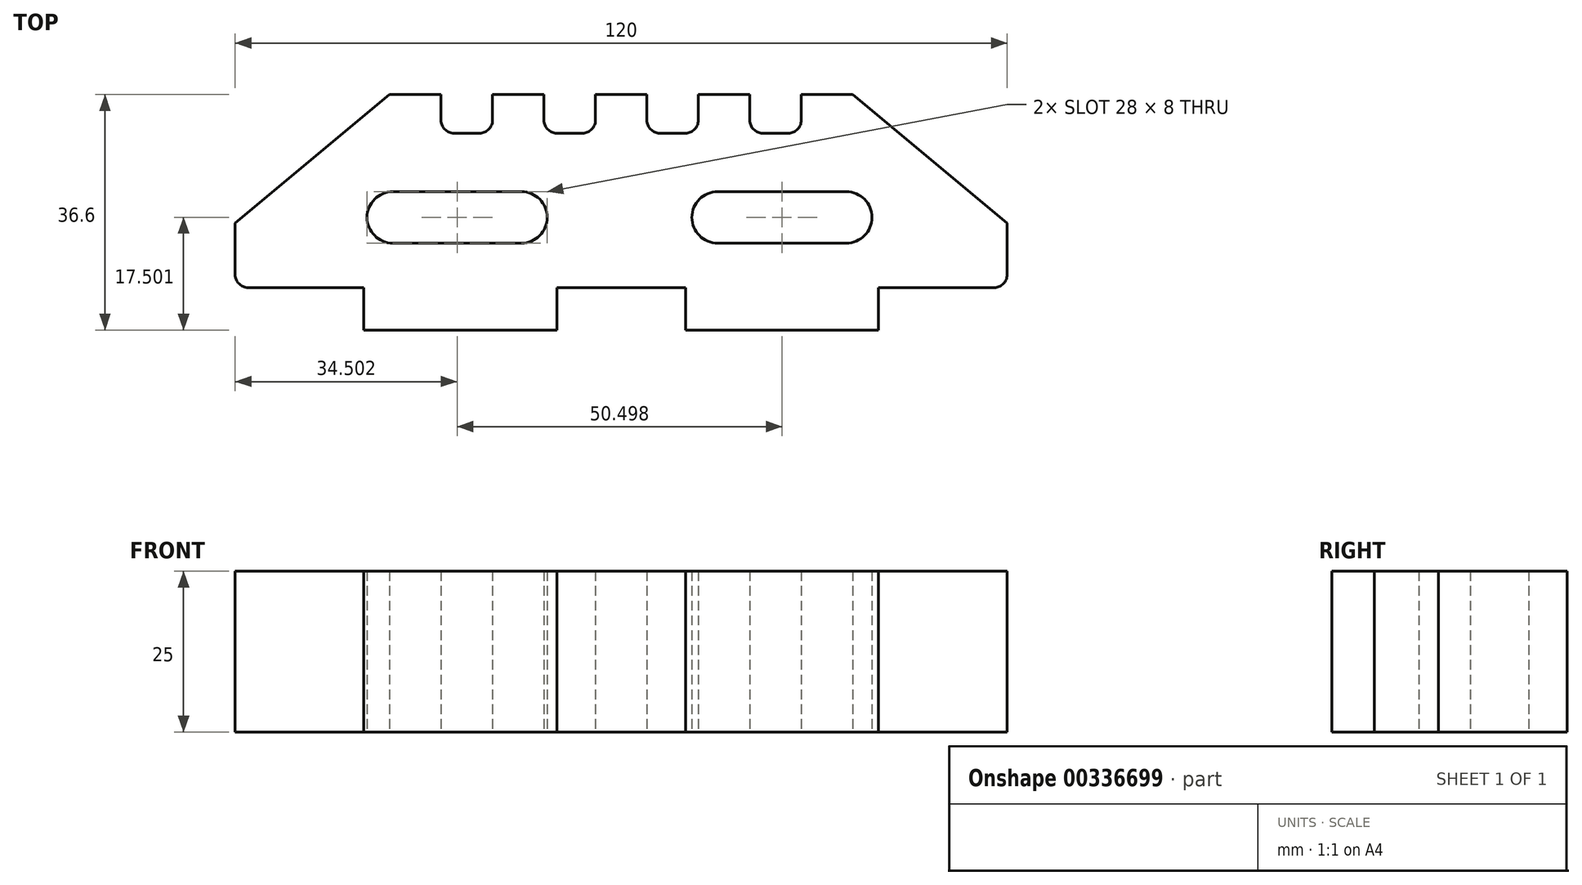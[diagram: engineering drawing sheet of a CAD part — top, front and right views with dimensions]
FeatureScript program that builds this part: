
annotation { "Feature Type Name" : "Feature", "Feature Type Description" : "" }
export const myFeature = defineFeature(function(context is Context, id is Id, definition is map)
    precondition{}
    {
        {
            var Q0;
            Q0=qCreatedBy(makeId("Top.planeOp"),FACE);
            var sketch = newSketch(context, id + "F0", { "sketchPlane" : qUnion([Q0])});
            skLineSegment(sketch, "E0", {"start": v(-86, -8.4) * mm, "end": v(-68, -8.4) * mm});
            skLineSegment(sketch, "E1", {"start": v(-68, -8.4) * mm, "end": v(-68, -15) * mm});
            skLineSegment(sketch, "E2", {"start": v(-68, -15) * mm, "end": v(-38, -15) * mm});
            skLineSegment(sketch, "E3", {"start": v(-38, -8.4) * mm, "end": v(-38, -15) * mm});
            skLineSegment(sketch, "E4", {"start": v(-38, -8.4) * mm, "end": v(-18, -8.4) * mm});
            skLineSegment(sketch, "E5", {"start": v(-18, -8.4) * mm, "end": v(-18, -15) * mm});
            skLineSegment(sketch, "E6", {"start": v(-18, -15) * mm, "end": v(12, -15) * mm});
            skLineSegment(sketch, "E7", {"start": v(12, -15) * mm, "end": v(12, -8.4) * mm});
            skLineSegment(sketch, "E8", {"start": v(12, -8.4) * mm, "end": v(30, -8.4) * mm});
            skLineSegment(sketch, "E9", {"start": v(-88, -6.4) * mm, "end": v(-88, 1.6) * mm});
            skLineSegment(sketch, "E10", {"start": v(-88, 1.6) * mm, "end": v(-64, 21.6) * mm});
            skLineSegment(sketch, "E11", {"start": v(-64, 21.6) * mm, "end": v(-56, 21.6) * mm});
            skLineSegment(sketch, "E12", {"start": v(-56, 21.6) * mm, "end": v(-56, 17.6) * mm});
            skLineSegment(sketch, "E13", {"start": v(-54, 15.6) * mm, "end": v(-50, 15.6) * mm});
            skLineSegment(sketch, "E14", {"start": v(-48, 17.6) * mm, "end": v(-48, 21.6) * mm});
            skLineSegment(sketch, "E15", {"start": v(-48, 21.6) * mm, "end": v(-40, 21.6) * mm});
            skLineSegment(sketch, "E16", {"start": v(-40, 21.6) * mm, "end": v(-40, 17.6) * mm});
            skLineSegment(sketch, "E17", {"start": v(-38, 15.6) * mm, "end": v(-34, 15.6) * mm});
            skLineSegment(sketch, "E18", {"start": v(-32, 17.6) * mm, "end": v(-32, 21.6) * mm});
            skLineSegment(sketch, "E19", {"start": v(-32, 21.6) * mm, "end": v(-24, 21.6) * mm});
            skPoint(sketch, "E20.end.orphan", {"position": v(-24.01, 15.6) * mm});
            skPoint(sketch, "E21.start.orphan", {"position": v(-7.45, 15.6) * mm});
            skPoint(sketch, "E22.start.orphan", {"position": v(-4.33, 21.6) * mm});
            skPoint(sketch, "E23.start.orphan", {"position": v(8.17, 15.6) * mm});
            skPoint(sketch, "E24.end.orphan", {"position": v(8, 21.6) * mm});
            skLineSegment(sketch, "E25", {"start": v(32, -6.4) * mm, "end": v(32, 1.6) * mm});
            skLineSegment(sketch, "E26", {"start": v(8, 21.6) * mm, "end": v(32, 1.6) * mm});
            skLineSegment(sketch, "E27", {"start": v(8, 21.6) * mm, "end": v(0, 21.6) * mm});
            skLineSegment(sketch, "E28", {"start": v(0, 21.6) * mm, "end": v(0, 17.6) * mm});
            skLineSegment(sketch, "E29", {"start": v(-2, 15.6) * mm, "end": v(-6, 15.6) * mm});
            skLineSegment(sketch, "E30", {"start": v(-8, 17.6) * mm, "end": v(-8, 21.6) * mm});
            skPoint(sketch, "E31.start.orphan", {"position": v(-20.13, 21.6) * mm});
            skLineSegment(sketch, "E32", {"start": v(-8, 21.6) * mm, "end": v(-16, 21.6) * mm});
            skLineSegment(sketch, "E33", {"start": v(-16, 17.6) * mm, "end": v(-16, 21.6) * mm});
            skLineSegment(sketch, "E34", {"start": v(-18, 15.6) * mm, "end": v(-22, 15.6) * mm});
            skLineSegment(sketch, "E35", {"start": v(-24, 17.6) * mm, "end": v(-24, 21.6) * mm});
            skPoint(sketch, "E36.visualSharp", {"position": v(-56, 15.6) * mm});
            skArc(sketch, "E36.filletArc", {"start": v(-56, 17.6) * mm, "mid": v(-55.41, 16.19) * mm, "end": v(-54, 15.6) * mm});
            skPoint(sketch, "E37.visualSharp", {"position": v(-48, 15.6) * mm});
            skArc(sketch, "E37.filletArc", {"start": v(-50, 15.6) * mm, "mid": v(-48.59, 16.19) * mm, "end": v(-48, 17.6) * mm});
            skPoint(sketch, "E38.visualSharp", {"position": v(-40, 15.6) * mm});
            skArc(sketch, "E38.filletArc", {"start": v(-40, 17.6) * mm, "mid": v(-39.41, 16.19) * mm, "end": v(-38, 15.6) * mm});
            skPoint(sketch, "E39.visualSharp", {"position": v(-32, 15.6) * mm});
            skArc(sketch, "E39.filletArc", {"start": v(-34, 15.6) * mm, "mid": v(-32.59, 16.19) * mm, "end": v(-32, 17.6) * mm});
            skPoint(sketch, "E40.visualSharp", {"position": v(-24, 15.6) * mm});
            skArc(sketch, "E40.filletArc", {"start": v(-24, 17.6) * mm, "mid": v(-23.41, 16.19) * mm, "end": v(-22, 15.6) * mm});
            skPoint(sketch, "E41.visualSharp", {"position": v(-16, 15.6) * mm});
            skArc(sketch, "E41.filletArc", {"start": v(-18, 15.6) * mm, "mid": v(-16.59, 16.19) * mm, "end": v(-16, 17.6) * mm});
            skPoint(sketch, "E42.visualSharp", {"position": v(-8, 15.6) * mm});
            skArc(sketch, "E42.filletArc", {"start": v(-8, 17.6) * mm, "mid": v(-7.41, 16.19) * mm, "end": v(-6, 15.6) * mm});
            skPoint(sketch, "E43.visualSharp", {"position": v(0, 15.6) * mm});
            skArc(sketch, "E43.filletArc", {"start": v(-2, 15.6) * mm, "mid": v(-0.59, 16.19) * mm, "end": v(0, 17.6) * mm});
            skPoint(sketch, "E44.visualSharp", {"position": v(-88, -8.4) * mm});
            skArc(sketch, "E44.filletArc", {"start": v(-88, -6.4) * mm, "mid": v(-87.41, -7.81) * mm, "end": v(-86, -8.4) * mm});
            skPoint(sketch, "E45.visualSharp", {"position": v(32, -8.4) * mm});
            skArc(sketch, "E45.filletArc", {"start": v(30, -8.4) * mm, "mid": v(31.41, -7.81) * mm, "end": v(32, -6.4) * mm});
            skLineSegment(sketch, "E46.bottom", {"start": v(-63.5, 6.5) * mm, "end": v(-43.5, 6.5) * mm});
            skLineSegment(sketch, "E46.top", {"start": v(-63.5, -1.5) * mm, "end": v(-43.5, -1.5) * mm});
            skLineSegment(sketch, "E46.left", {"start": v(-67.5, 2.5) * mm, "end": v(-67.5, 2.5) * mm});
            skLineSegment(sketch, "E46.right", {"start": v(-39.5, 2.5) * mm, "end": v(-39.5, 2.5) * mm});
            skLineSegment(sketch, "E47.bottom", {"start": v(-13, 6.5) * mm, "end": v(7, 6.5) * mm});
            skLineSegment(sketch, "E47.top", {"start": v(-13, -1.5) * mm, "end": v(7, -1.5) * mm});
            skLineSegment(sketch, "E47.left", {"start": v(-17, 2.5) * mm, "end": v(-17, 2.5) * mm});
            skLineSegment(sketch, "E47.right", {"start": v(11, 2.5) * mm, "end": v(11, 2.5) * mm});
            skLineSegment(sketch, "E48", {"start": v(-28, 21.6) * mm, "end": v(-28, -8.4) * mm});
            skLineSegment(sketch, "E49", {"start": v(-39.5, -1.5) * mm, "end": v(-17, -1.5) * mm});
            skPoint(sketch, "E50.visualSharp", {"position": v(-67.5, 6.5) * mm});
            skArc(sketch, "E50.filletArc", {"start": v(-63.5, 6.5) * mm, "mid": v(-66.33, 5.33) * mm, "end": v(-67.5, 2.5) * mm});
            skPoint(sketch, "E51.visualSharp", {"position": v(-67.5, -1.5) * mm});
            skArc(sketch, "E51.filletArc", {"start": v(-67.5, 2.5) * mm, "mid": v(-66.33, -0.33) * mm, "end": v(-63.5, -1.5) * mm});
            skPoint(sketch, "E52.visualSharp", {"position": v(-39.5, 6.5) * mm});
            skArc(sketch, "E52.filletArc", {"start": v(-39.5, 2.5) * mm, "mid": v(-40.67, 5.33) * mm, "end": v(-43.5, 6.5) * mm});
            skPoint(sketch, "E53.visualSharp", {"position": v(-39.5, -1.5) * mm});
            skArc(sketch, "E53.filletArc", {"start": v(-43.5, -1.5) * mm, "mid": v(-40.67, -0.33) * mm, "end": v(-39.5, 2.5) * mm});
            skPoint(sketch, "E54.visualSharp", {"position": v(-17, 6.5) * mm});
            skArc(sketch, "E54.filletArc", {"start": v(-13, 6.5) * mm, "mid": v(-15.83, 5.33) * mm, "end": v(-17, 2.5) * mm});
            skPoint(sketch, "E55.visualSharp", {"position": v(-17, -1.5) * mm});
            skArc(sketch, "E55.filletArc", {"start": v(-17, 2.5) * mm, "mid": v(-15.83, -0.33) * mm, "end": v(-13, -1.5) * mm});
            skPoint(sketch, "E56.visualSharp", {"position": v(11, 6.5) * mm});
            skArc(sketch, "E56.filletArc", {"start": v(11, 2.5) * mm, "mid": v(9.83, 5.33) * mm, "end": v(7, 6.5) * mm});
            skPoint(sketch, "E57.visualSharp", {"position": v(11, -1.5) * mm});
            skArc(sketch, "E57.filletArc", {"start": v(7, -1.5) * mm, "mid": v(9.83, -0.33) * mm, "end": v(11, 2.5) * mm});
            skSolve(sketch);
        }
        {
            var Q0;
            Q0 = qSketchRegion(id + "F0", true);
            extrude(context, id + "F1", {"entities" : qUnion([Q0]), "depth" : 25 * mm});
        }
    });
